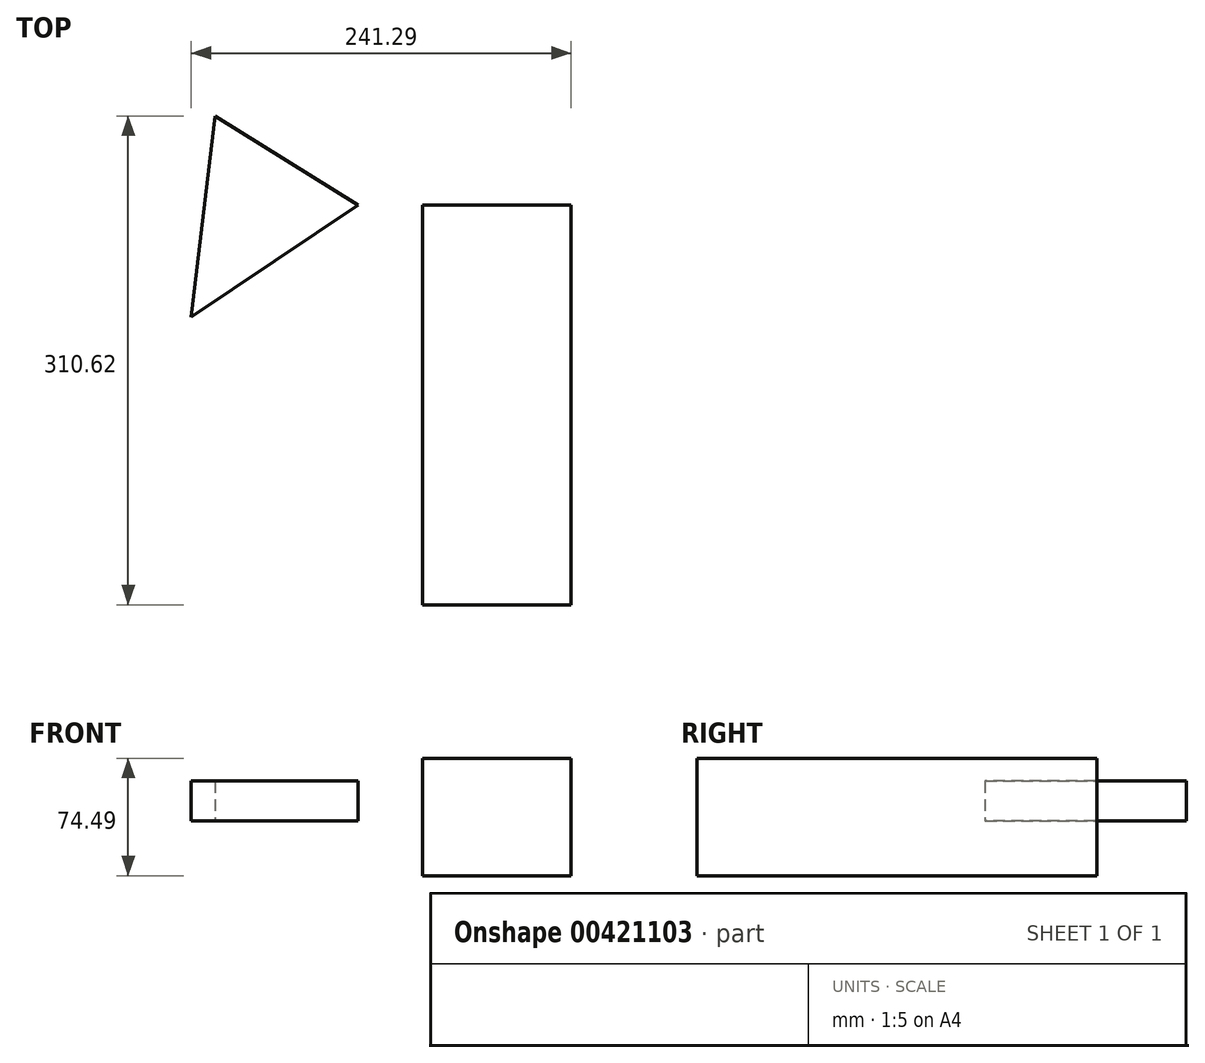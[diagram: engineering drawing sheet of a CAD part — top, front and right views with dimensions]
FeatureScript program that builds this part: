
annotation { "Feature Type Name" : "Feature", "Feature Type Description" : "" }
export const myFeature = defineFeature(function(context is Context, id is Id, definition is map)
    precondition{}
    {
        {
            var Q0;
            Q0=qCreatedBy(makeId("Front.planeOp"),FACE);
            var sketch = newSketch(context, id + "F0", { "sketchPlane" : qUnion([Q0])});
            skLineSegment(sketch, "E0.bottom", {"start": v(-48.08, 39.8) * mm, "end": v(46.31, 39.8) * mm});
            skLineSegment(sketch, "E0.top", {"start": v(-48.08, -34.68) * mm, "end": v(46.31, -34.68) * mm});
            skLineSegment(sketch, "E0.left", {"start": v(-48.08, 39.8) * mm, "end": v(-48.08, -34.68) * mm});
            skLineSegment(sketch, "E0.right", {"start": v(46.31, 39.8) * mm, "end": v(46.31, -34.68) * mm});
            skSolve(sketch);
        }
        {
            var Q0;
            Q0 = qSketchRegion(id + "F0", true);
            extrude(context, id + "F1", {"entities" : qUnion([Q0]), "depth" : 254 * mm});
        }
        {
            var Q0;
            Q0=qCreatedBy(makeId("Top.planeOp"),FACE);
            var sketch = newSketch(context, id + "F2", { "sketchPlane" : qUnion([Q0])});
            skLineSegment(sketch, "E1", {"start": v(-179.98, 56.62) * mm, "end": v(-194.98, -71.16) * mm});
            skLineSegment(sketch, "E2", {"start": v(-194.98, -71.16) * mm, "end": v(-89.05, 0) * mm});
            skLineSegment(sketch, "E3", {"start": v(-89.05, 0) * mm, "end": v(-179.98, 56.62) * mm});
            skSolve(sketch);
        }
        {
            var Q0;
            Q0=makeQuery(id+"F2.imprint","IMPRINT",FACE,{"disambiguationData":[TD([[makeQuery(id+"F2.imprint","IMPRINT",EDGE,{"derivedFrom":sQuery(id+"F2.wireOp",EDGE,"E1")}),1.0]])]});
            extrude(context, id + "F3", {"entities" : qUnion([Q0]), "depth" : 25.4 * mm});
        }
    });
